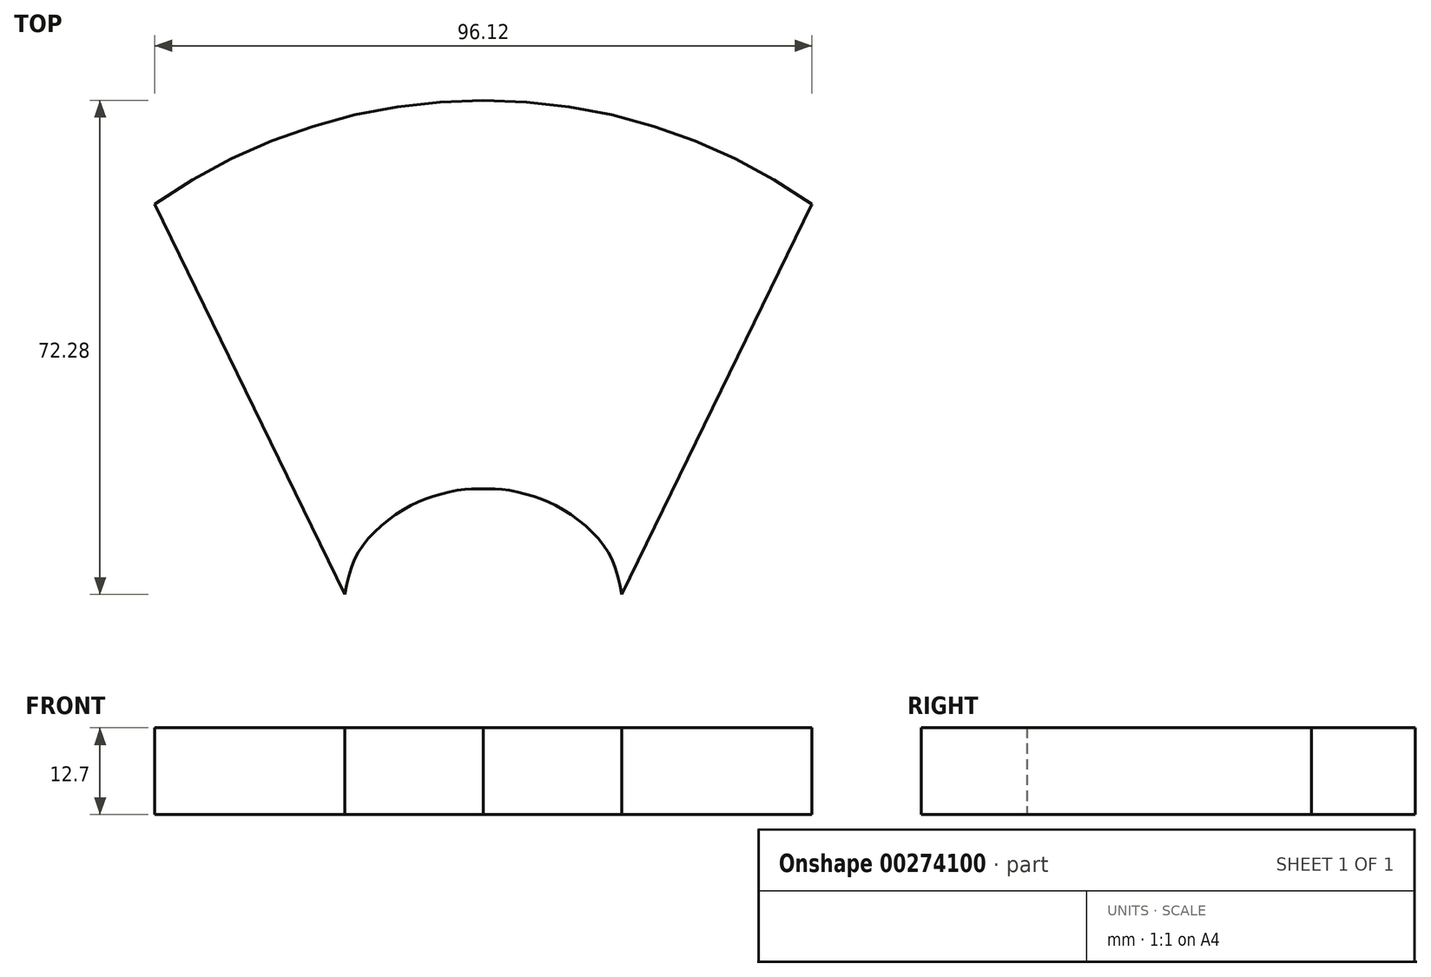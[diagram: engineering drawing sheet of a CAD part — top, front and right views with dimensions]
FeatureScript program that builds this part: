
annotation { "Feature Type Name" : "Feature", "Feature Type Description" : "" }
export const myFeature = defineFeature(function(context is Context, id is Id, definition is map)
    precondition{}
    {
        {
            var Q0;
            Q0=qCreatedBy(makeId("Top.planeOp"),FACE);
            var sketch = newSketch(context, id + "F0", { "sketchPlane" : qUnion([Q0])});
            skFitSpline(sketch, "E0", {"points": [v(-20.27, 0) * mm, v(-18.75, 5.33) * mm, v(-15.7, 9.33) * mm, v(-11.13, 12.75) * mm, v(-6.95, 14.46) * mm, v(-2.57, 15.42) * mm, v(0, 15.42) * mm], "startDerivative": vector(6.3, 30.56) * mm, "endDerivative": vector(19.09, -1.18) * mm});
            skFitSpline(sketch, "E1.MirrorCS", {"points": [v(20.27, 0) * mm, v(18.75, 5.33) * mm, v(15.7, 9.33) * mm, v(11.13, 12.75) * mm, v(6.95, 14.46) * mm, v(2.57, 15.42) * mm, v(0, 15.42) * mm], "startDerivative": vector(-6.3, 30.56) * mm, "endDerivative": vector(-19.09, -1.18) * mm});
            skLineSegment(sketch, "E2", {"start": v(-20.27, 0) * mm, "end": v(-48.06, 57.1) * mm});
            skLineSegment(sketch, "E3.MirrorCS", {"start": v(20.27, 0) * mm, "end": v(48.06, 57.1) * mm});
            skArc(sketch, "E4", {"start": v(48.06, 57.1) * mm, "mid": v(0, 72.28) * mm, "end": v(-48.06, 57.1) * mm});
            skSolve(sketch);
        }
        {
            var Q0;
            Q0 = qSketchRegion(id + "F0", true);
            extrude(context, id + "F1", {"entities" : qUnion([Q0]), "depth" : 12.7 * mm});
        }
    });
